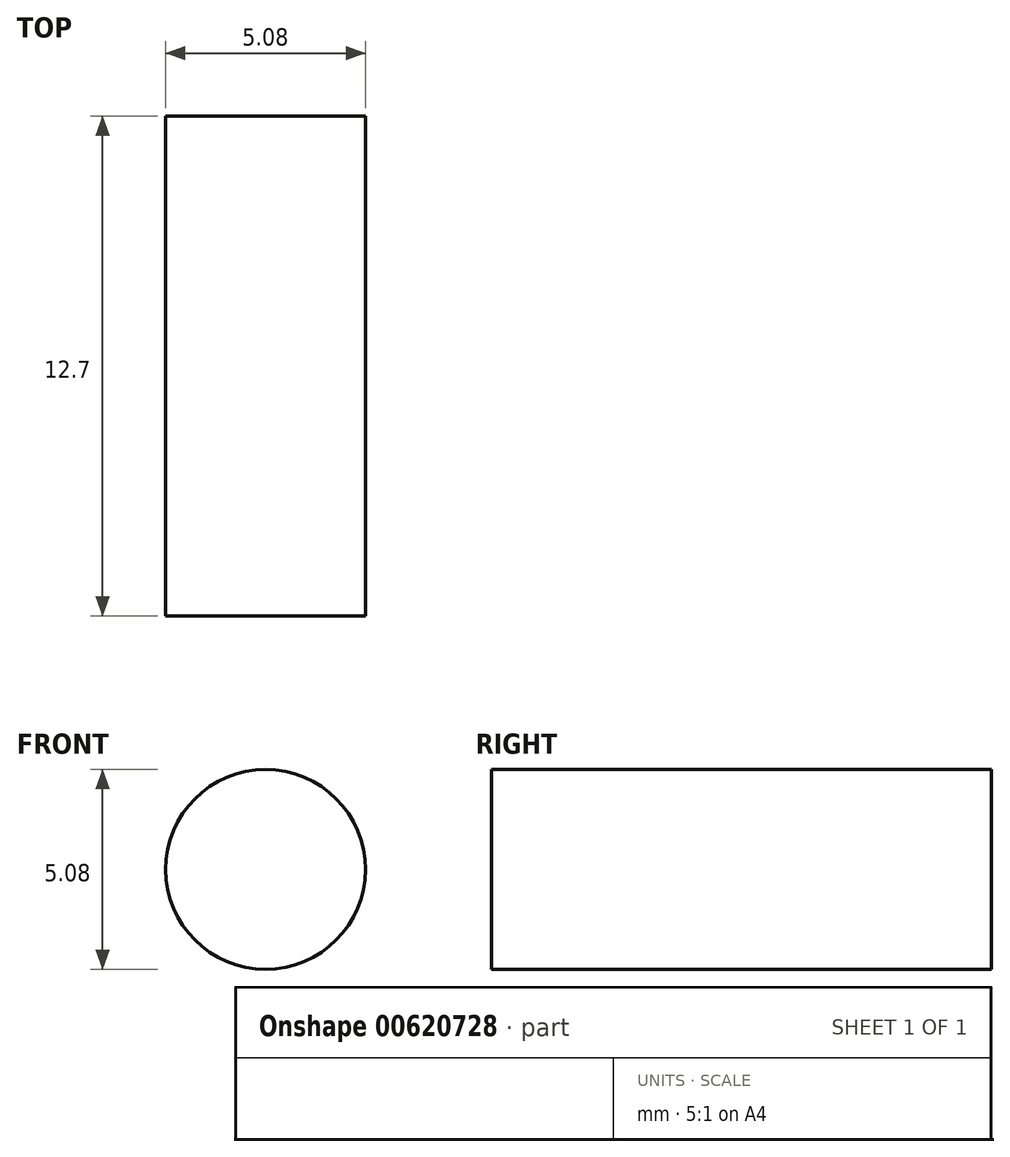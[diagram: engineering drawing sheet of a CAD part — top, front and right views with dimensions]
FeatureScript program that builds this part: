
annotation { "Feature Type Name" : "Feature", "Feature Type Description" : "" }
export const myFeature = defineFeature(function(context is Context, id is Id, definition is map)
    precondition{}
    {
        {
            var Q0;
            Q0=qCreatedBy(makeId("Front.planeOp"),FACE);
            var sketch = newSketch(context, id + "F0", { "sketchPlane" : qUnion([Q0])});
            skCircle(sketch, "E0", {"center": v(0, 0) * mm, "radius": 2.54 * mm});
            skSolve(sketch);
        }
        {
            var Q0;
            Q0 = qSketchRegion(id + "F0", true);
            extrude(context, id + "F1", {"entities" : qUnion([Q0]), "depth" : 12.7 * mm, "offsetDistance" : 25.4 * mm});
        }
    });
